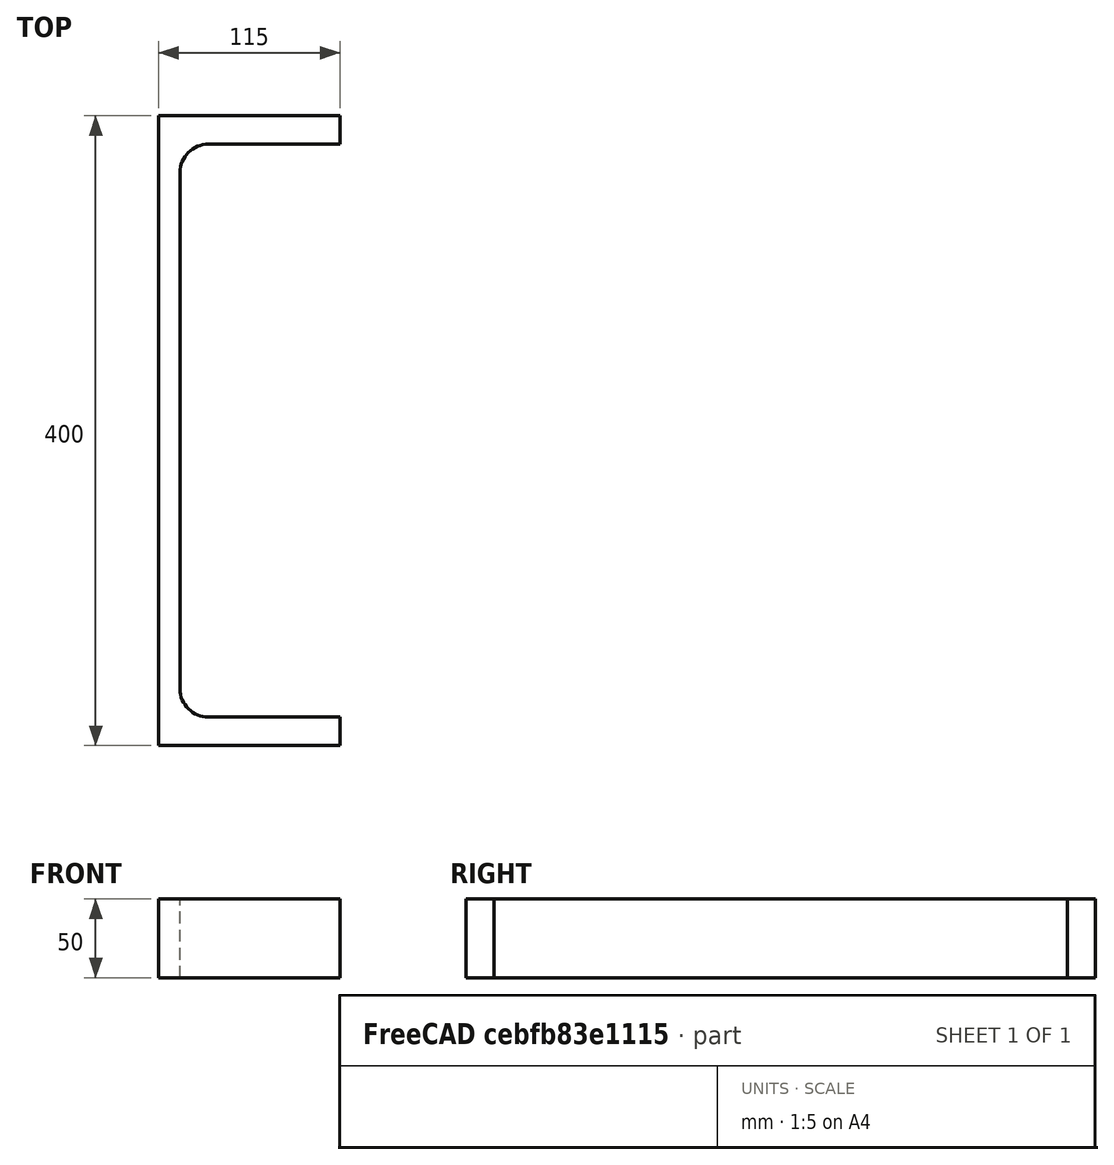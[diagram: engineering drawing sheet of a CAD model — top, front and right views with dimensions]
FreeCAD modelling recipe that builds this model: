
FCSTD DOCUMENT  (FreeCAD 0.20R29410 (Git))
Label: UPE-Profile 400 DIN1026-2 S235JR
License: All rights reserved
LicenseURL: http://en.wikipedia.org/wiki/All_rights_reserved
objects: Sketcher::SketchObject×1, Part::Extrusion×1
note: 2 computed .brp shape members not serialized (recipe doc carries the construction recipe); baked Part::Feature solids carry a one-line shape summary decoded from their .brp

FEATURE [Sketcher::SketchObject] Sketch
  FullyConstrained = true
  MapMode = 5
  sketch-geometry (10):
    g0: LineSegment StartX=13.5 StartY=-164 StartZ=0 EndX=13.5 EndY=164 EndZ=0
    g1: LineSegment StartX=31.5 StartY=182 StartZ=0 EndX=115 EndY=182 EndZ=0
    g2: LineSegment StartX=115 StartY=182 StartZ=0 EndX=115 EndY=200 EndZ=0
    g3: LineSegment StartX=115 StartY=-200 StartZ=0 EndX=115 EndY=-182 EndZ=0
    g4: LineSegment StartX=115 StartY=-182 StartZ=0 EndX=31.5 EndY=-182 EndZ=0
    g5: ArcOfCircle CenterX=31.5 CenterY=164 CenterZ=0 NormalX=0 NormalY=0 NormalZ=1 AngleXU=0 Radius=18 StartAngle=1.5708 EndAngle=3.14159
    g6: ArcOfCircle CenterX=31.5 CenterY=-164 CenterZ=0 NormalX=0 NormalY=0 NormalZ=1 AngleXU=0 Radius=18 StartAngle=3.14159 EndAngle=4.71239
    g7: LineSegment StartX=115 StartY=-200 StartZ=0 EndX=0 EndY=-200 EndZ=0
    g8: LineSegment StartX=0 StartY=-200 StartZ=0 EndX=0 EndY=200 EndZ=0
    g9: LineSegment StartX=0 StartY=200 StartZ=0 EndX=115 EndY=200 EndZ=0
  constraints (27):
    c: Vertical(g0)
    c: Coincident(g2,g1)
    c: Vertical(g2)
    c: Vertical(g3)
    c: Coincident(g4,g3)
    c: Horizontal(g4)
    c: Tangent(g1,g5) = 1.5708
    c: Tangent(g0,g5) = 1.5708
    c: Tangent(g0,g6) = 1.5708
    c: Tangent(g4,g6) = 1.5708
    c: Symmetric(g2,g3,g-1)
    c: DistanceY(g2) = 18
    c: Radius(g5) = 18
    c: Coincident(g3,g7)
    c: PointOnObject(g7,g-2)
    c: Horizontal(g7)
    c: Coincident(g7,g8)
    c: PointOnObject(g8,g-2)
    c: Coincident(g8,g9)
    c: Coincident(g9,g2)
    c: Horizontal(g9)
    c: Distance(g-1,g0) = 13.5
    c: DistanceX(g9,g9) = 115
    c: Horizontal(g1)
    c: Equal(g3,g2)
    c: Equal(g5,g6)
    c: DistanceY(g3,g2) = 400
FEATURE [Part::Extrusion] Extrude  label="UPE-Profile 400 DIN1026-2 S235JR"
  Base = -> Sketch
  Dir = (0,0,50)
  DirMode = 0
  FaceMakerClass = Part::FaceMakerExtrusion
  LengthFwd = 0
  LengthRev = 0
  Solid = true
  Symmetric = false
